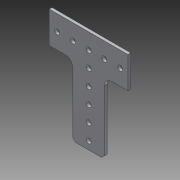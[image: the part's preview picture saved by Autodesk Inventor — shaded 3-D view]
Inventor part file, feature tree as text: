
AUTODESK INVENTOR PART (.ipt)
format: ipt  version: 2014 SP1 (Build 180222100, 222)  size: 165,888 bytes
history: native  units: in
note: dims shown in document units (in); Inventor stores cm internally (conversion verified against a paired STEP export)
features: other x2, extrude x1, imported_body x1, sketch x1
ambient origin geometry x8: Origin, YZ Plane, XZ Plane, XY Plane, X Axis, Y Axis, Z Axis, Center Point
bodies: Body1 (feature_tree)
feature tree (5):
  other  "Break-Corner1"
  other  "217-3547-STEP1"
  extrude  "Extrusion1"  Depth=0.75in
  imported_body  "Base1"
  sketch  "Sketch1"  dims[d0=0.75in d1=0.75in d2=1.0in d3=0.0in]
